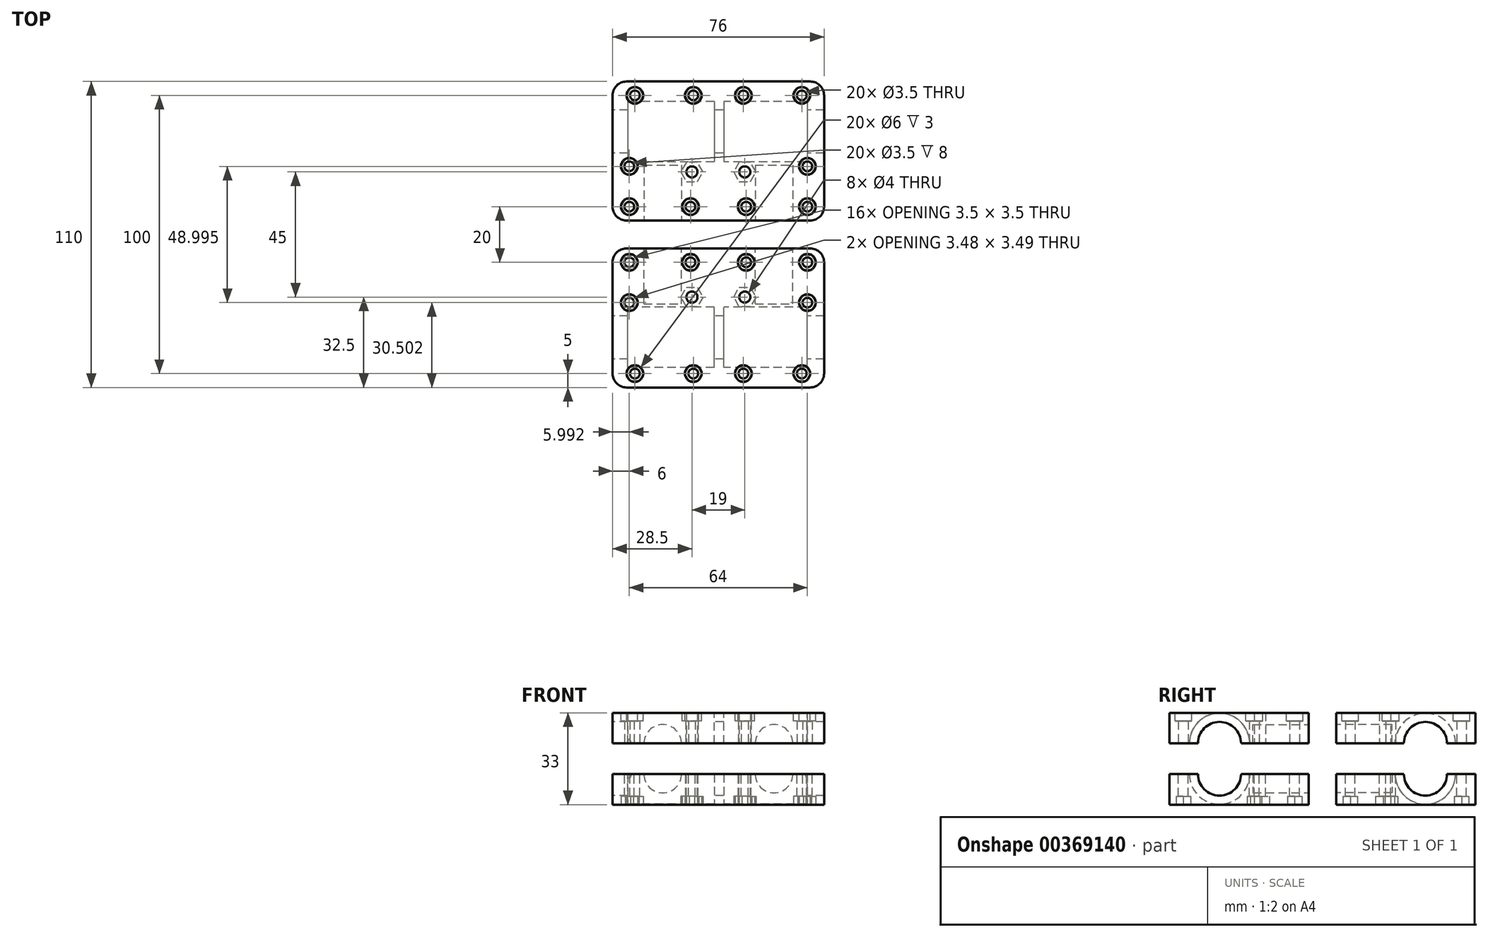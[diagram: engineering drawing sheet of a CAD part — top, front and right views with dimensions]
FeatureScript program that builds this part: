
annotation { "Feature Type Name" : "Feature", "Feature Type Description" : "" }
export const myFeature = defineFeature(function(context is Context, id is Id, definition is map)
    precondition{}
    {
        {
            var Q0;
            Q0=qCreatedBy(makeId("Top.planeOp"),FACE);
            var sketch = newSketch(context, id + "F0", { "sketchPlane" : qUnion([Q0])});
            skLineSegment(sketch, "E0.bottom", {"start": v(38, -25) * mm, "end": v(-38, -25) * mm});
            skLineSegment(sketch, "E0.top", {"start": v(38, 25) * mm, "end": v(-38, 25) * mm});
            skLineSegment(sketch, "E0.left", {"start": v(38, -25) * mm, "end": v(38, 25) * mm});
            skLineSegment(sketch, "E0.right", {"start": v(-38, -25) * mm, "end": v(-38, 25) * mm});
            skPoint(sketch, "E0.middle", {"position": v(0, 0) * mm});
            skSolve(sketch);
        }
        {
            var Q0;
            Q0=qSketchRegion(id+"F0",true);
            extrude(context, id + "F1", {"entities" : qUnion([Q0]), "endBound" : BoundingType.SYMMETRIC, "depth" : 11 * mm});
        }
        {
            var Q0;
            Q0=makeQuery(id+"F1.opExtrude","CAP_FACE",FACE,{"disambiguationData":[OSD([sQuery(id+"F0.wireOp",EDGE,"E0.bottom"),sQuery(id+"F0.wireOp",EDGE,"E0.top"),sQuery(id+"F0.wireOp",EDGE,"E0.left"),sQuery(id+"F0.wireOp",EDGE,"E0.right")])],"isStart":false});
            var sketch = newSketch(context, id + "F2", { "sketchPlane" : qUnion([Q0])});
            skCircle(sketch, "E1", {"center": v(-30, 20) * mm, "radius": 1.75 * mm});
            skCircle(sketch, "E2", {"center": v(-9, 20) * mm, "radius": 1.75 * mm});
            skCircle(sketch, "E3", {"center": v(9, 20) * mm, "radius": 1.75 * mm});
            skCircle(sketch, "E4", {"center": v(30, 20) * mm, "radius": 1.75 * mm});
            skCircle(sketch, "E5", {"center": v(-32, -20) * mm, "radius": 1.75 * mm});
            skCircle(sketch, "E6", {"center": v(-10, -20) * mm, "radius": 1.75 * mm});
            skCircle(sketch, "E7", {"center": v(10, -20) * mm, "radius": 1.75 * mm});
            skCircle(sketch, "E8", {"center": v(32, -20) * mm, "radius": 1.75 * mm});
            skCircle(sketch, "E9", {"center": v(32, -5.5) * mm, "radius": 1.75 * mm});
            skCircle(sketch, "E10", {"center": v(-9.5, -7.5) * mm, "radius": 2 * mm});
            skCircle(sketch, "E11", {"center": v(9.5, -7.5) * mm, "radius": 2 * mm});
            skCircle(sketch, "E12", {"center": v(-32, -5.5) * mm, "radius": 1.75 * mm});
            skSolve(sketch);
        }
        {
            var Q0;
            Q0=qSketchRegion(id+"F2",true);
            extrude(context, id + "F3", {"entities" : qUnion([Q0]), "operationType" : NewBodyOperationType.REMOVE, "endBound" : BoundingType.THROUGH_ALL, "oppositeDirection" : true, "depth" : 25 * mm});
        }
        {
            var Q0;
            Q0=makeQuery(id+"F1.opExtrude","SWEPT_FACE",FACE,{"disambiguationData":[OSD([sQuery(id+"F0.wireOp",EDGE,"E0.bottom")])]});
            var sketch = newSketch(context, id + "F4", { "sketchPlane" : qUnion([Q0])});
            skCircle(sketch, "E13", {"center": v(-20, 5.5) * mm, "radius": 6.75 * mm});
            skCircle(sketch, "E14", {"center": v(20, 5.5) * mm, "radius": 6.75 * mm});
            skSolve(sketch);
        }
        {
            var Q0;
            Q0=qSketchRegion(id+"F4",true);
            extrude(context, id + "F5", {"entities" : qUnion([Q0]), "operationType" : NewBodyOperationType.REMOVE, "oppositeDirection" : true, "depth" : 20 * mm});
        }
        {
            var Q0;
            Q0=makeQuery(id+"F1.opExtrude","CAP_FACE",FACE,{"disambiguationData":[OSD([sQuery(id+"F0.wireOp",EDGE,"E0.bottom"),sQuery(id+"F0.wireOp",EDGE,"E0.top"),sQuery(id+"F0.wireOp",EDGE,"E0.left"),sQuery(id+"F0.wireOp",EDGE,"E0.right")])],"isStart":true});
            var sketch = newSketch(context, id + "F6", { "sketchPlane" : qUnion([Q0])});
            skCircle(sketch, "E15.cCircle", {"center": v(-32, 20) * mm, "radius": 2.6 * mm, "construction": true});
            skLineSegment(sketch, "E15.0", {"start": v(-30.5, 17.4) * mm, "end": v(-33.5, 17.4) * mm});
            skLineSegment(sketch, "E15.1", {"start": v(-33.5, 17.4) * mm, "end": v(-35, 20) * mm});
            skLineSegment(sketch, "E15.2", {"start": v(-35, 20) * mm, "end": v(-33.5, 22.6) * mm});
            skLineSegment(sketch, "E15.3", {"start": v(-33.5, 22.6) * mm, "end": v(-30.5, 22.6) * mm});
            skLineSegment(sketch, "E15.4", {"start": v(-30.5, 22.6) * mm, "end": v(-29, 20) * mm});
            skLineSegment(sketch, "E15.5", {"start": v(-29, 20) * mm, "end": v(-30.5, 17.4) * mm});
            skPoint(sketch, "E15.0.midPoint", {"position": v(-32, 17.4) * mm});
            skCircle(sketch, "E16.cCircle", {"center": v(10, 20) * mm, "radius": 2.6 * mm, "construction": true});
            skLineSegment(sketch, "E16.0", {"start": v(11.5, 17.4) * mm, "end": v(8.5, 17.4) * mm});
            skLineSegment(sketch, "E16.1", {"start": v(8.5, 17.4) * mm, "end": v(7, 20) * mm});
            skLineSegment(sketch, "E16.2", {"start": v(7, 20) * mm, "end": v(8.5, 22.6) * mm});
            skLineSegment(sketch, "E16.3", {"start": v(8.5, 22.6) * mm, "end": v(11.5, 22.6) * mm});
            skLineSegment(sketch, "E16.4", {"start": v(11.5, 22.6) * mm, "end": v(13, 20) * mm});
            skLineSegment(sketch, "E16.5", {"start": v(13, 20) * mm, "end": v(11.5, 17.4) * mm});
            skPoint(sketch, "E16.0.midPoint", {"position": v(10, 17.4) * mm});
            skCircle(sketch, "E17.cCircle", {"center": v(-10, 20) * mm, "radius": 2.6 * mm, "construction": true});
            skLineSegment(sketch, "E17.0", {"start": v(-8.5, 17.4) * mm, "end": v(-11.5, 17.4) * mm});
            skLineSegment(sketch, "E17.1", {"start": v(-11.5, 17.4) * mm, "end": v(-13, 20) * mm});
            skLineSegment(sketch, "E17.2", {"start": v(-13, 20) * mm, "end": v(-11.5, 22.6) * mm});
            skLineSegment(sketch, "E17.3", {"start": v(-11.5, 22.6) * mm, "end": v(-8.5, 22.6) * mm});
            skLineSegment(sketch, "E17.4", {"start": v(-8.5, 22.6) * mm, "end": v(-7, 20) * mm});
            skLineSegment(sketch, "E17.5", {"start": v(-7, 20) * mm, "end": v(-8.5, 17.4) * mm});
            skPoint(sketch, "E17.0.midPoint", {"position": v(-10, 17.4) * mm});
            skCircle(sketch, "E18.cCircle", {"center": v(32, 20) * mm, "radius": 2.6 * mm, "construction": true});
            skLineSegment(sketch, "E18.0", {"start": v(33.5, 17.4) * mm, "end": v(30.5, 17.4) * mm});
            skLineSegment(sketch, "E18.1", {"start": v(30.5, 17.4) * mm, "end": v(29, 20) * mm});
            skLineSegment(sketch, "E18.2", {"start": v(29, 20) * mm, "end": v(30.5, 22.6) * mm});
            skLineSegment(sketch, "E18.3", {"start": v(30.5, 22.6) * mm, "end": v(33.5, 22.6) * mm});
            skLineSegment(sketch, "E18.4", {"start": v(33.5, 22.6) * mm, "end": v(35, 20) * mm});
            skLineSegment(sketch, "E18.5", {"start": v(35, 20) * mm, "end": v(33.5, 17.4) * mm});
            skPoint(sketch, "E18.0.midPoint", {"position": v(32, 17.4) * mm});
            skCircle(sketch, "E19.cCircle", {"center": v(-32, 5.5) * mm, "radius": 2.6 * mm, "construction": true});
            skLineSegment(sketch, "E19.0", {"start": v(-30.5, 2.9) * mm, "end": v(-33.5, 2.9) * mm});
            skLineSegment(sketch, "E19.1", {"start": v(-33.5, 2.9) * mm, "end": v(-35, 5.5) * mm});
            skLineSegment(sketch, "E19.2", {"start": v(-35, 5.5) * mm, "end": v(-33.5, 8.1) * mm});
            skLineSegment(sketch, "E19.3", {"start": v(-33.5, 8.1) * mm, "end": v(-30.5, 8.1) * mm});
            skLineSegment(sketch, "E19.4", {"start": v(-30.5, 8.1) * mm, "end": v(-29, 5.5) * mm});
            skLineSegment(sketch, "E19.5", {"start": v(-29, 5.5) * mm, "end": v(-30.5, 2.9) * mm});
            skPoint(sketch, "E19.0.midPoint", {"position": v(-32, 2.9) * mm});
            skCircle(sketch, "E20.cCircle", {"center": v(-30, -20) * mm, "radius": 2.6 * mm, "construction": true});
            skLineSegment(sketch, "E20.0", {"start": v(-28.5, -22.6) * mm, "end": v(-31.5, -22.6) * mm});
            skLineSegment(sketch, "E20.1", {"start": v(-31.5, -22.6) * mm, "end": v(-33, -20) * mm});
            skLineSegment(sketch, "E20.2", {"start": v(-33, -20) * mm, "end": v(-31.5, -17.4) * mm});
            skLineSegment(sketch, "E20.3", {"start": v(-31.5, -17.4) * mm, "end": v(-28.5, -17.4) * mm});
            skLineSegment(sketch, "E20.4", {"start": v(-28.5, -17.4) * mm, "end": v(-27, -20) * mm});
            skLineSegment(sketch, "E20.5", {"start": v(-27, -20) * mm, "end": v(-28.5, -22.6) * mm});
            skPoint(sketch, "E20.0.midPoint", {"position": v(-30, -22.6) * mm});
            skCircle(sketch, "E21.cCircle", {"center": v(-9, -20) * mm, "radius": 2.6 * mm, "construction": true});
            skLineSegment(sketch, "E21.0", {"start": v(-7.5, -22.6) * mm, "end": v(-10.5, -22.6) * mm});
            skLineSegment(sketch, "E21.1", {"start": v(-10.5, -22.6) * mm, "end": v(-12, -20) * mm});
            skLineSegment(sketch, "E21.2", {"start": v(-12, -20) * mm, "end": v(-10.5, -17.4) * mm});
            skLineSegment(sketch, "E21.3", {"start": v(-10.5, -17.4) * mm, "end": v(-7.5, -17.4) * mm});
            skLineSegment(sketch, "E21.4", {"start": v(-7.5, -17.4) * mm, "end": v(-6, -20) * mm});
            skLineSegment(sketch, "E21.5", {"start": v(-6, -20) * mm, "end": v(-7.5, -22.6) * mm});
            skPoint(sketch, "E21.0.midPoint", {"position": v(-9, -22.6) * mm});
            skCircle(sketch, "E22.cCircle", {"center": v(9, -20) * mm, "radius": 2.6 * mm, "construction": true});
            skLineSegment(sketch, "E22.0", {"start": v(10.5, -22.6) * mm, "end": v(7.5, -22.6) * mm});
            skLineSegment(sketch, "E22.1", {"start": v(7.5, -22.6) * mm, "end": v(6, -20) * mm});
            skLineSegment(sketch, "E22.2", {"start": v(6, -20) * mm, "end": v(7.5, -17.4) * mm});
            skLineSegment(sketch, "E22.3", {"start": v(7.5, -17.4) * mm, "end": v(10.5, -17.4) * mm});
            skLineSegment(sketch, "E22.4", {"start": v(10.5, -17.4) * mm, "end": v(12, -20) * mm});
            skLineSegment(sketch, "E22.5", {"start": v(12, -20) * mm, "end": v(10.5, -22.6) * mm});
            skPoint(sketch, "E22.0.midPoint", {"position": v(9, -22.6) * mm});
            skCircle(sketch, "E23.cCircle", {"center": v(30, -20) * mm, "radius": 2.6 * mm, "construction": true});
            skLineSegment(sketch, "E23.0", {"start": v(31.5, -22.6) * mm, "end": v(28.5, -22.6) * mm});
            skLineSegment(sketch, "E23.1", {"start": v(28.5, -22.6) * mm, "end": v(27, -20) * mm});
            skLineSegment(sketch, "E23.2", {"start": v(27, -20) * mm, "end": v(28.5, -17.4) * mm});
            skLineSegment(sketch, "E23.3", {"start": v(28.5, -17.4) * mm, "end": v(31.5, -17.4) * mm});
            skLineSegment(sketch, "E23.4", {"start": v(31.5, -17.4) * mm, "end": v(33, -20) * mm});
            skLineSegment(sketch, "E23.5", {"start": v(33, -20) * mm, "end": v(31.5, -22.6) * mm});
            skPoint(sketch, "E23.0.midPoint", {"position": v(30, -22.6) * mm});
            skCircle(sketch, "E24.cCircle", {"center": v(32, 5.5) * mm, "radius": 2.6 * mm, "construction": true});
            skLineSegment(sketch, "E24.0", {"start": v(33.5, 2.9) * mm, "end": v(30.5, 2.9) * mm});
            skLineSegment(sketch, "E24.1", {"start": v(30.5, 2.9) * mm, "end": v(29, 5.5) * mm});
            skLineSegment(sketch, "E24.2", {"start": v(29, 5.5) * mm, "end": v(30.5, 8.1) * mm});
            skLineSegment(sketch, "E24.3", {"start": v(30.5, 8.1) * mm, "end": v(33.5, 8.1) * mm});
            skLineSegment(sketch, "E24.4", {"start": v(33.5, 8.1) * mm, "end": v(35, 5.5) * mm});
            skLineSegment(sketch, "E24.5", {"start": v(35, 5.5) * mm, "end": v(33.5, 2.9) * mm});
            skPoint(sketch, "E24.0.midPoint", {"position": v(32, 2.9) * mm});
            skSolve(sketch);
        }
        {
            var Q0;
            Q0=qSketchRegion(id+"F6",true);
            extrude(context, id + "F7", {"entities" : qUnion([Q0]), "operationType" : NewBodyOperationType.REMOVE, "oppositeDirection" : true, "depth" : 3 * mm});
        }
        {
            var Q0;
            Q0=makeQuery(id+"F1.opExtrude","SWEPT_FACE",FACE,{"disambiguationData":[OSD([sQuery(id+"F0.wireOp",EDGE,"E0.right")])]});
            var sketch = newSketch(context, id + "F8", { "sketchPlane" : qUnion([Q0])});
            skCircle(sketch, "E25", {"center": v(-7, 5.5) * mm, "radius": 7.75 * mm});
            skSolve(sketch);
        }
        {
            var Q0;
            Q0=qSketchRegion(id+"F8",true);
            extrude(context, id + "F9", {"entities" : qUnion([Q0]), "operationType" : NewBodyOperationType.REMOVE, "endBound" : BoundingType.THROUGH_ALL, "oppositeDirection" : true, "depth" : 25 * mm});
        }
        {
            var Q0;
            Q0=makeQuery(id+"F1.opExtrude","SWEPT_FACE",FACE,{"disambiguationData":[OSD([sQuery(id+"F0.wireOp",EDGE,"E0.right")])]});
            var sketch = newSketch(context, id + "F10", { "sketchPlane" : qUnion([Q0])});
            skCircle(sketch, "E26", {"center": v(-7, 5.5) * mm, "radius": 10.85 * mm});
            skSolve(sketch);
        }
        {
            var Q0;
            Q0=qSketchRegion(id+"F10",true);
            extrude(context, id + "F11", {"entities" : qUnion([Q0]), "operationType" : NewBodyOperationType.REMOVE, "oppositeDirection" : true, "depth" : 36.5 * mm, "hasSecondDirection" : true, "secondDirectionOppositeDirection" : true, "secondDirectionDepth" : 5.5 * mm});
        }
        {
            var Q0;
            Q0=makeQuery(id+"F1.opExtrude","SWEPT_EDGE",EDGE,{"disambiguationData":[OSD([sQuery(id+"F0.wireOp",EDGE,"E0.bottom"),sQuery(id+"F0.wireOp",EDGE,"E0.left")])]});
            var Q1;
            Q1=makeQuery(id+"F1.opExtrude","SWEPT_EDGE",EDGE,{"disambiguationData":[OSD([sQuery(id+"F0.wireOp",EDGE,"E0.bottom"),sQuery(id+"F0.wireOp",EDGE,"E0.right")])]});
            var Q2;
            Q2=makeQuery(id+"F1.opExtrude","SWEPT_EDGE",EDGE,{"disambiguationData":[OSD([sQuery(id+"F0.wireOp",EDGE,"E0.top"),sQuery(id+"F0.wireOp",EDGE,"E0.right")])]});
            var Q3;
            Q3=makeQuery(id+"F1.opExtrude","SWEPT_EDGE",EDGE,{"disambiguationData":[OSD([sQuery(id+"F0.wireOp",EDGE,"E0.top"),sQuery(id+"F0.wireOp",EDGE,"E0.left")])]});
            fillet(context, id + "F12", {"entities" : qUnion([Q0, Q1, Q2, Q3]), "radius" : 5 * mm, "tangentPropagation" : true, "allowEdgeOverflow" : false});
        }
        {
            var Q0;
            Q0=qSketchRegion(id+"F10",true);
            extrude(context, id + "F13", {"entities" : qUnion([Q0]), "operationType" : NewBodyOperationType.REMOVE, "oppositeDirection" : true, "depth" : 70 * mm, "hasSecondDirection" : true, "secondDirectionOppositeDirection" : true, "secondDirectionDepth" : 40 * mm});
        }
        {
            var Q0;
            Q0=qCreatedBy(makeId("Top.planeOp"),FACE);
            cPlane(context, id + "F14", {"entities" : qUnion([Q0]), "cplaneType" : CPlaneType.OFFSET, "offset" : 11 * mm, "width" : 150 * mm, "height" : 150 * mm});
        }
        {
            var Q0;
            Q0=makeQuery(id+"F1.opExtrude","SWEPT_BODY",BODY,{"disambiguationData":[OSD([sQuery(id+"F0.wireOp",EDGE,"E0.bottom"),sQuery(id+"F0.wireOp",EDGE,"E0.top"),sQuery(id+"F0.wireOp",EDGE,"E0.left"),sQuery(id+"F0.wireOp",EDGE,"E0.right")])]});
            var Q1;
            Q1=qCreatedBy(id+"F14.planeOp",FACE);
            mirror(context, id + "F15", {"entities" : qUnion([Q0]), "mirrorPlane" : qUnion([Q1])});
        }
        {
            var Q0;
            Q0=makeQuery(id+"F15.opPattern","COPY",FACE,{"derivedFrom":makeQuery(id+"F1.opExtrude","CAP_FACE",FACE,{"disambiguationData":[OSD([sQuery(id+"F0.wireOp",EDGE,"E0.bottom"),sQuery(id+"F0.wireOp",EDGE,"E0.top"),sQuery(id+"F0.wireOp",EDGE,"E0.left"),sQuery(id+"F0.wireOp",EDGE,"E0.right")])],"isStart":true}),"instanceName":"1"});
            var sketch = newSketch(context, id + "F16", { "sketchPlane" : qUnion([Q0])});
            skCircle(sketch, "E27", {"center": v(-30, 20) * mm, "radius": 3 * mm});
            skCircle(sketch, "E28", {"center": v(-9, 20) * mm, "radius": 3 * mm});
            skCircle(sketch, "E29", {"center": v(-49.47, 3.97) * mm, "radius": 3 * mm});
            skCircle(sketch, "E30", {"center": v(-32, -5.5) * mm, "radius": 3 * mm});
            skCircle(sketch, "E31", {"center": v(-32, -20) * mm, "radius": 3 * mm});
            skCircle(sketch, "E32", {"center": v(32, -5.5) * mm, "radius": 3 * mm});
            skCircle(sketch, "E33", {"center": v(32, -20) * mm, "radius": 3 * mm});
            skCircle(sketch, "E34", {"center": v(10, -20) * mm, "radius": 3 * mm});
            skCircle(sketch, "E35", {"center": v(-10, -20) * mm, "radius": 3 * mm});
            skCircle(sketch, "E36", {"center": v(30, 20) * mm, "radius": 3 * mm});
            skCircle(sketch, "E37", {"center": v(9, 20) * mm, "radius": 3 * mm});
            skSolve(sketch);
        }
        {
            var Q0;
            Q0=qSketchRegion(id+"F16",true);
            extrude(context, id + "F17", {"entities" : qUnion([Q0]), "operationType" : NewBodyOperationType.REMOVE, "oppositeDirection" : true, "depth" : 3 * mm});
        }
        {
            var Q0;
            Q0=makeQuery(id+"F6.imprint","IMPRINT",FACE,{"disambiguationData":[TD([[makeQuery(id+"F6.imprint","IMPRINT",EDGE,{"derivedFrom":sQuery(id+"F6.wireOp",EDGE,"E15.0")}),1.0]])]});
            var sketch = newSketch(context, id + "F18", { "sketchPlane" : qUnion([Q0])});
            skCircle(sketch, "E38.cCircle", {"center": v(-9.5, 7.5) * mm, "radius": 3.46 * mm, "construction": true});
            skLineSegment(sketch, "E38.0", {"start": v(-7.5, 4.04) * mm, "end": v(-11.5, 4.04) * mm});
            skLineSegment(sketch, "E38.1", {"start": v(-11.5, 4.04) * mm, "end": v(-13.5, 7.5) * mm});
            skLineSegment(sketch, "E38.2", {"start": v(-13.5, 7.5) * mm, "end": v(-11.5, 10.96) * mm});
            skLineSegment(sketch, "E38.3", {"start": v(-11.5, 10.96) * mm, "end": v(-7.5, 10.96) * mm});
            skLineSegment(sketch, "E38.4", {"start": v(-7.5, 10.96) * mm, "end": v(-5.5, 7.5) * mm});
            skLineSegment(sketch, "E38.5", {"start": v(-5.5, 7.5) * mm, "end": v(-7.5, 4.04) * mm});
            skPoint(sketch, "E38.0.midPoint", {"position": v(-9.5, 4.04) * mm});
            skCircle(sketch, "E39.cCircle", {"center": v(9.5, 7.5) * mm, "radius": 3.46 * mm, "construction": true});
            skLineSegment(sketch, "E39.0", {"start": v(11.5, 4.04) * mm, "end": v(7.5, 4.04) * mm});
            skLineSegment(sketch, "E39.1", {"start": v(7.5, 4.04) * mm, "end": v(5.5, 7.5) * mm});
            skLineSegment(sketch, "E39.2", {"start": v(5.5, 7.5) * mm, "end": v(7.5, 10.96) * mm});
            skLineSegment(sketch, "E39.3", {"start": v(7.5, 10.96) * mm, "end": v(11.5, 10.96) * mm});
            skLineSegment(sketch, "E39.4", {"start": v(11.5, 10.96) * mm, "end": v(13.5, 7.5) * mm});
            skLineSegment(sketch, "E39.5", {"start": v(13.5, 7.5) * mm, "end": v(11.5, 4.04) * mm});
            skPoint(sketch, "E39.0.midPoint", {"position": v(9.5, 4.04) * mm});
            skSolve(sketch);
        }
        {
            var Q0;
            Q0=qSketchRegion(id+"F18",true);
            extrude(context, id + "F19", {"entities" : qUnion([Q0]), "operationType" : NewBodyOperationType.REMOVE, "oppositeDirection" : true, "depth" : 3 * mm});
        }
        {
            var Q0;
            Q0=qCreatedBy(makeId("Front.planeOp"),FACE);
            cPlane(context, id + "F20", {"entities" : qUnion([Q0]), "cplaneType" : CPlaneType.OFFSET, "offset" : 30 * mm, "width" : 150 * mm, "height" : 150 * mm});
        }
        {
            var Q0;
            Q0=makeQuery(id+"F15.opPattern","COPY",BODY,{"derivedFrom":makeQuery(id+"F1.opExtrude","SWEPT_BODY",BODY,{"disambiguationData":[OSD([sQuery(id+"F0.wireOp",EDGE,"E0.bottom"),sQuery(id+"F0.wireOp",EDGE,"E0.top"),sQuery(id+"F0.wireOp",EDGE,"E0.left"),sQuery(id+"F0.wireOp",EDGE,"E0.right")])]}),"instanceName":"1"});
            var Q1;
            Q1=makeQuery(id+"F1.opExtrude","SWEPT_BODY",BODY,{"disambiguationData":[OSD([sQuery(id+"F0.wireOp",EDGE,"E0.bottom"),sQuery(id+"F0.wireOp",EDGE,"E0.top"),sQuery(id+"F0.wireOp",EDGE,"E0.left"),sQuery(id+"F0.wireOp",EDGE,"E0.right")])]});
            var Q2;
            Q2=qCreatedBy(id+"F20.planeOp",FACE);
            mirror(context, id + "F21", {"entities" : qUnion([Q0, Q1]), "mirrorPlane" : qUnion([Q2])});
        }
    });
